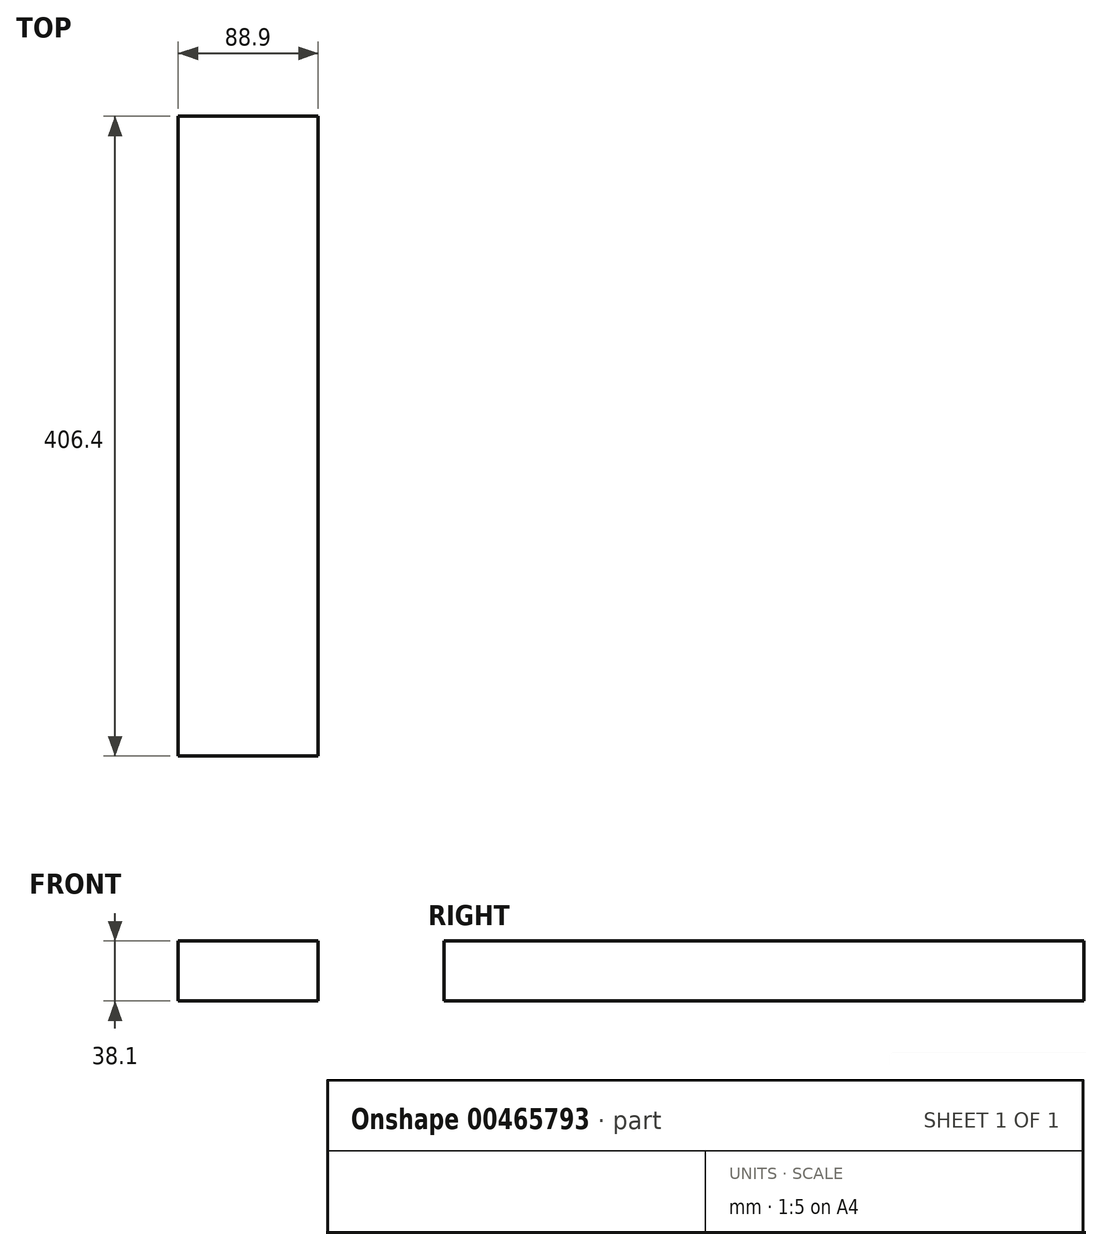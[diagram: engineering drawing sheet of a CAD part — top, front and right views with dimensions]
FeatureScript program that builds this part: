
annotation { "Feature Type Name" : "Feature", "Feature Type Description" : "" }
export const myFeature = defineFeature(function(context is Context, id is Id, definition is map)
    precondition{}
    {
        {
            var Q0;
            Q0=qCreatedBy(makeId("Front.planeOp"),FACE);
            var sketch = newSketch(context, id + "F0", { "sketchPlane" : qUnion([Q0])});
            skLineSegment(sketch, "E0.bottom", {"start": v(44.45, 19.05) * mm, "end": v(-44.45, 19.05) * mm});
            skLineSegment(sketch, "E0.top", {"start": v(44.45, -19.05) * mm, "end": v(-44.45, -19.05) * mm});
            skLineSegment(sketch, "E0.left", {"start": v(44.45, 19.05) * mm, "end": v(44.45, -19.05) * mm});
            skLineSegment(sketch, "E0.right", {"start": v(-44.45, 19.05) * mm, "end": v(-44.45, -19.05) * mm});
            skPoint(sketch, "E0.middle", {"position": v(0, 0) * mm});
            skSolve(sketch);
        }
        {
            var Q0;
            Q0=makeQuery(id+"F0.imprint","IMPRINT",FACE,{"disambiguationData":[TD([[makeQuery(id+"F0.imprint","IMPRINT",EDGE,{"derivedFrom":sQuery(id+"F0.wireOp",EDGE,"E0.bottom")}),1.0]])]});
            extrude(context, id + "F1", {"entities" : qUnion([Q0]), "endBound" : BoundingType.SYMMETRIC, "depth" : 406.4 * mm});
        }
    });
